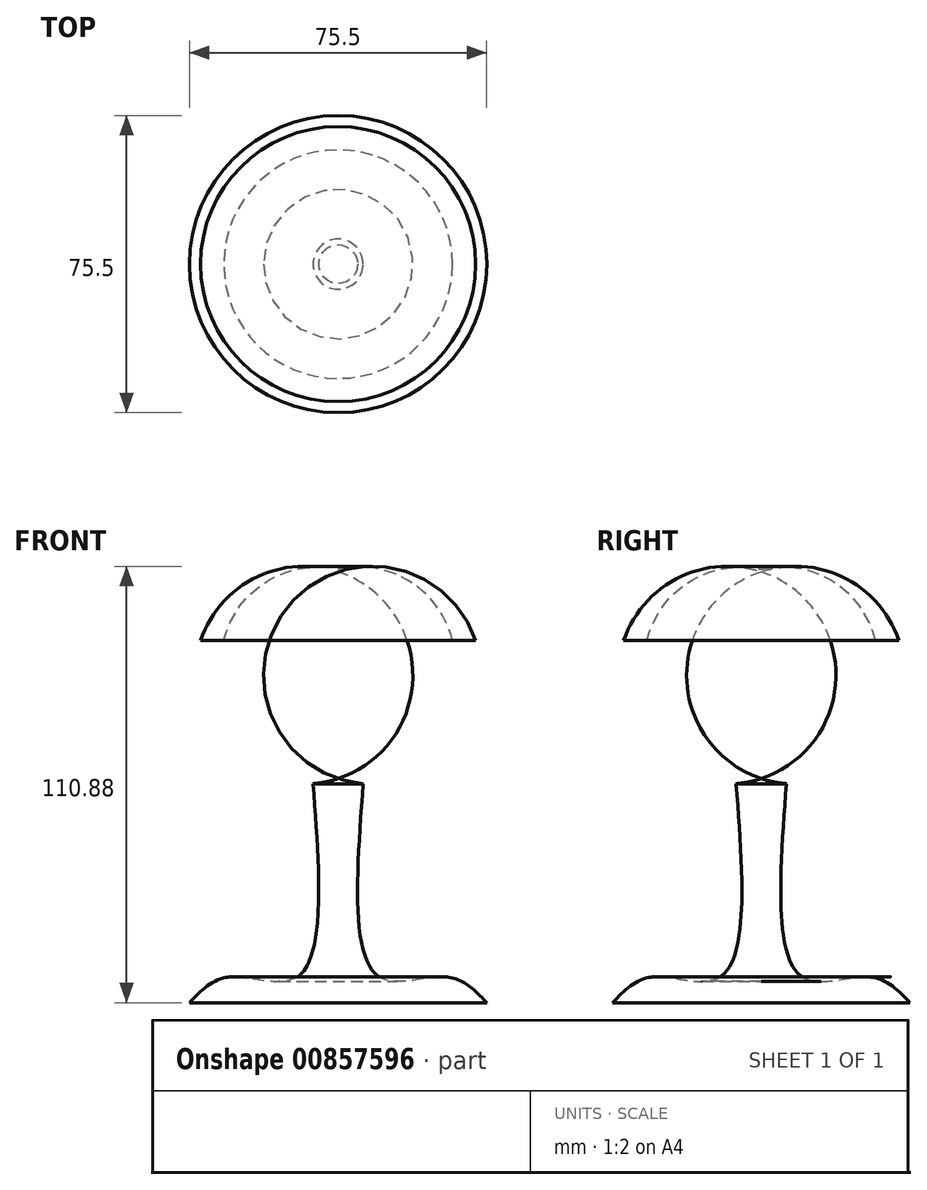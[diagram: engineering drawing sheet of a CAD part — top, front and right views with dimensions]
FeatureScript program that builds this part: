
annotation { "Feature Type Name" : "Feature", "Feature Type Description" : "" }
export const myFeature = defineFeature(function(context is Context, id is Id, definition is map)
    precondition{}
    {
        {
            var Q0;
            Q0=qCreatedBy(makeId("Front.planeOp"),FACE);
            var sketch = newSketch(context, id + "F0", { "sketchPlane" : qUnion([Q0])});
            skLineSegment(sketch, "E0", {"start": v(0, 29.2) * mm, "end": v(0, -55.62) * mm});
            skLineSegment(sketch, "E1", {"start": v(0, -55.62) * mm, "end": v(-37.75, -55.62) * mm});
            skFitSpline(sketch, "E2", {"points": [v(-37.75, -55.62) * mm, v(-27.5, -49.1) * mm, v(-10.4, -49.1) * mm, v(-6.37, 0) * mm], "startDerivative": vector(36.52, 38.57) * mm, "endDerivative": vector(-10.4, 138.78) * mm});
            skArc(sketch, "E3", {"start": v(-34.96, 36.35) * mm, "mid": v(-30.46, 10.47) * mm, "end": v(-6.37, 0) * mm});
            skLineSegment(sketch, "E4", {"start": v(-34.96, 36.35) * mm, "end": v(-29.05, 36.35) * mm});
            skArc(sketch, "E5", {"start": v(-29.05, 36.35) * mm, "mid": v(-22.72, 13.53) * mm, "end": v(0, 6.84) * mm});
            skSolve(sketch);
        }
        {
            var Q0;
            {var subQ0=sQuery(id+"F0.wireOp",EDGE,"E1");Q0=makeQuery(id+"F0.imprint","IMPRINT",FACE,{"disambiguationData":[TD([[makeQuery(id+"F0.imprint","IMPRINT",EDGE,{"derivedFrom":subQ0}),-1.0]])]});}
            var Q1;
            Q1=sQuery(id+"F0.wireOp",EDGE,"E0");
            revolve(context, id + "F1", {"surfaceOperationType" : NewSurfaceOperationType.NEW, "entities" : qUnion([Q0]), "axis" : qUnion([Q1]), "revolveType" : RevolveType.FULL});
        }
    });
